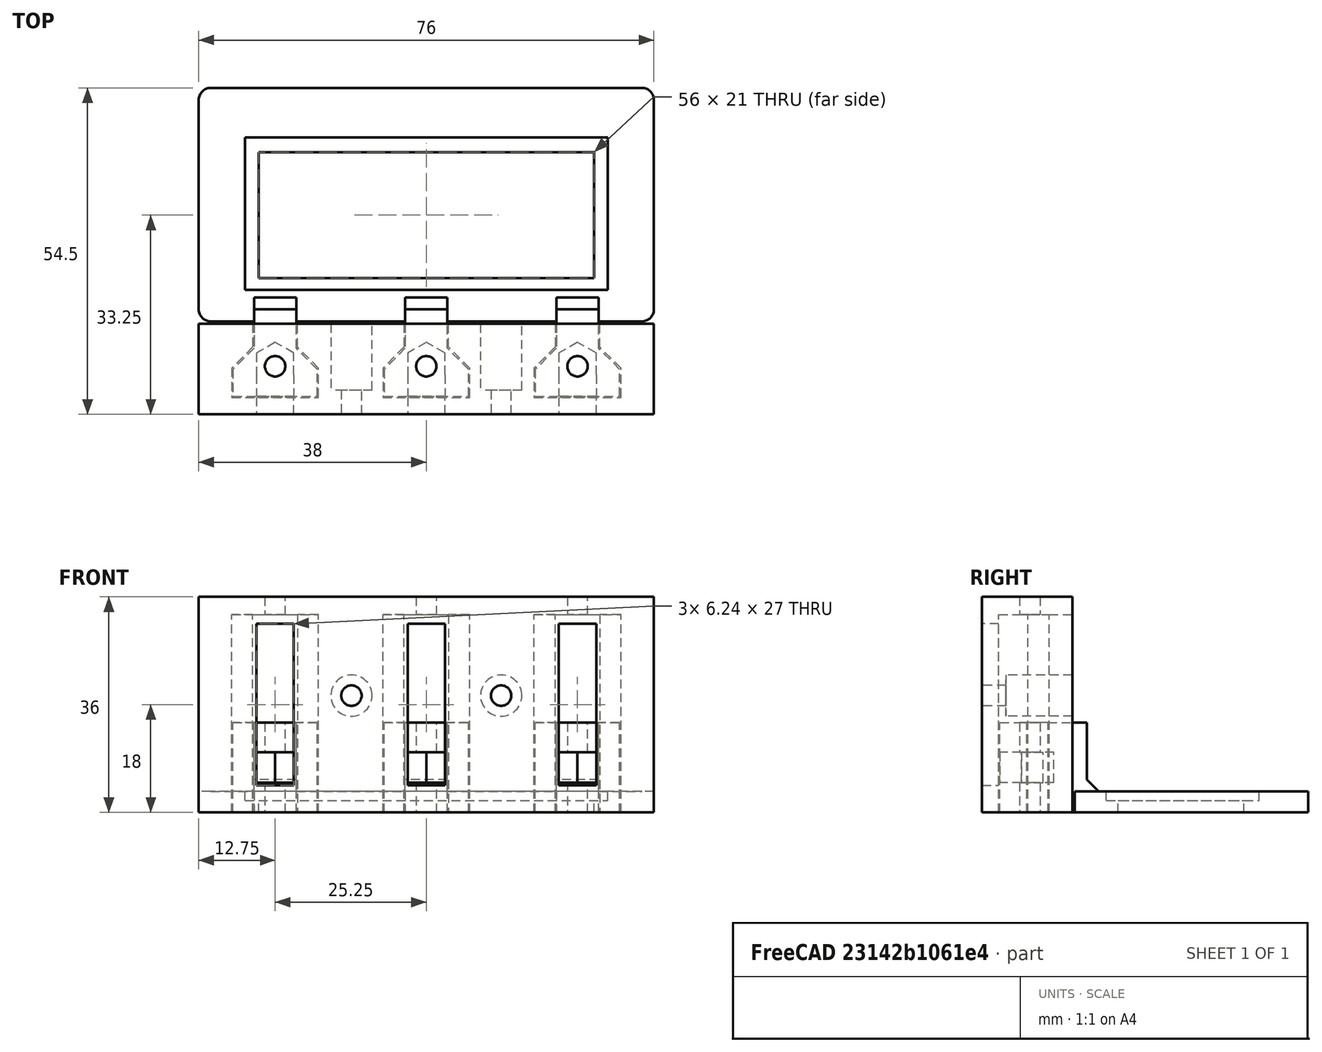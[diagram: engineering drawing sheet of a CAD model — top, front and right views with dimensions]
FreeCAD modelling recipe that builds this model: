
FCSTD DOCUMENT  (FreeCAD 0.16R6706 (Git))
Label: linfiltersup
License: All rights reserved
LicenseURL: http://en.wikipedia.org/wiki/All_rights_reserved
objects: Part::Feature×3, Part::FeaturePython×2, Part::Prism×1, Part::Box×1, Part::Fuse×1, Part::Cut×1, Part::MultiFuse×1, Part::Chamfer×1
note: 11 computed .brp shape members not serialized (recipe doc carries the construction recipe); baked Part::Feature solids carry a one-line shape summary decoded from their .brp

FEATURE [Part::Prism] nuthole_nut
  Circumradius = 3.605
  Height = 5.04
  Placement = pos=(0,0,0) rot=(-0.57735,0.57735,0.57735;2.0944rad)
  Polygon = 6
FEATURE [Part::Box] nuthole_hole
  Height = 9.4
  Length = 6.24386
  Placement = pos=(-3.12193,0,0) rot=(0,0,1;0rad)
  Width = 5.04
FEATURE [Part::Fuse] nuthole
  Base = -> nuthole_nut
  Placement = pos=(0,8.4,4.98) rot=(1,0,0;1.5708rad)
  Tool = -> nuthole_hole
FEATURE [Part::Feature] block
  shape: bbox 14.1 x 14.5 x 15 mm, 11 faces (baked)
FEATURE [Part::Cut] blocknut
  Base = -> block
  Tool = -> nuthole
FEATURE [Part::FeaturePython] Clone  label="blocknut0"  # Draft clone (typed FeaturePython)
  Objects = -> [blocknut]
  Placement = pos=(-25.25,0,0) rot=(0,0,1;0rad)
  Scale = (1,1,1)
FEATURE [Part::FeaturePython] Clone001  label="blocknut1"  # Draft clone (typed FeaturePython)
  Objects = -> [blocknut]
  Placement = pos=(25.25,0,0) rot=(0,0,1;0rad)
  Scale = (1,1,1)
FEATURE [Part::Feature] filter_basehole
  shape: bbox 76 x 39 x 3.5 mm, 19 faces (baked)
FEATURE [Part::MultiFuse] filtermov
  Shapes = -> [filter_basehole,blocknut,Clone,Clone001]
FEATURE [Part::Chamfer] filtermovchmf
  Base = -> filtermov
  Edges = 3 edges r=2: [Edge12,Edge16,Edge20]
FEATURE [Part::Feature] fix_support
  shape: bbox 76 x 15.1 x 36 mm, 51 faces (baked)
